# Revit family: Accessories-Teknion-HDAS_Framed_Fabric_Add_On_For_Open_Shelves_Kiosk-R2021
name_source: partatom
category: Furniture
units: mm (PartAtom-declared; Revit-internal decimal feet)

## family parameters
Always vertical = Yes
Cut with Voids When Loaded = No
OmniClass Number = 23.40.20.00
OmniClass Title = General Furniture and Specialties
Room Calculation Point = No
Shared = Yes
Work Plane-Based = No

## types (2) — shared parameters
Assembly Code = E2020200
Manufacturer = Teknion
Manufacturer Fax = 416.661.4586
Part Number = HDAS
Product Documentation Link = https://assets.teknion.com
Product Line = Kiosk
Product Page URL = https://www.teknion.com
Series = Kiosk
Sustainability Data = https://www.teknion.com
URL = www.teknion.com
Unit Weight URL = http://www.teknion.com
Warranty = http://www.teknion.com
zero-valued in all types: Default Elevation

## per-type parameters (varying)
| type | Description | Height 1 | Height 2 | Model |
| Height 48" | Framed Fabric Add On For Open Shelves Kiosk - Height 48", Width 30" | 72.42 " | 24.67 " | HDAS4830 |
| Height 67" | Framed Fabric Add On For Open Shelves Kiosk - Height 67", Width 30" | 71.58 " | 4.83 " | HDAS6730 |

## geometry (parser evidence)
native form markers: Sweep x3
no freeform markers — native parametric forms only
